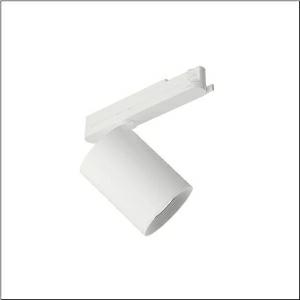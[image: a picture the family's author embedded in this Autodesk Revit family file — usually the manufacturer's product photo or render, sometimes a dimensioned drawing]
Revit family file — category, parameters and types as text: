
# Revit family: spot_21_51se13mbb5b
name_source: partatom
category: Lighting Fixtures
units: mm (PartAtom-declared; Revit-internal decimal feet)

## family parameters
Cut with Voids When Loaded = No
Host = Face
Light Source = No
Part Type = Normal
Room Calculation Point = No
Round Connector Dimension = Use Diameter
Shared = No

## types (1)
- --- (1 x LED, 5350 lm, 41.8 W, 3000K)
    Apparent Load = 42 VA
    CIE Flux Codes = 95 98 99 100 100
    Color Rendering = 90
    Color Temperature = 3000K
    Default Elevation = 1800 mm
    Description = Spot 21, directional spotlight, light control with lens, of PMMA, LED rated luminous flux: 5.140lm, light colour: 930, control gear: ECG Multilumen, with 3-phase adapter, mains connection: 220..240V, AC, 50/60Hz, of aluminium, traffic white (RAL 9016), length: 213mm, diameter: 105mm, protection rating (complete): IP20, insulation class (complete): insulation class I (protective earthing), certification: CE, impact resistance: IK02, permissible ambient temperature for indoor applications: -20..+40°C, packaging unit: 1 piece
    Height = 175 mm
    Lamp = 1 x LED
    Lamp Light Flux = 5350 lm
    Lamp Power = 41.8 W
    Lamp count = 1
    Length = 105 mm
    Luminous efficacy = 128 lm/W
    Manufacturer = Siteco
    ModVariant = No
    Model = 51SE13MBB5B
    Mounting Place = Ceiling
    Mounting Type = Pendant
    Number of Poles = 1
    OnlyDefault = Yes
    Power Factor = 1
    Product Name = Spot 21
    Product group = directional spotlight
    ProductGroupID = 904
    Protection Class = Protection class I
    Protection Degree = IP 20
    RLX_Detail_Level = 1
    RlxData = <blob elided: 17669 chars, md5=89f1b0f4>
    Socket = socket
    Standby Power = 0 W
    System Light Flux = 5350 lm
    System Power = 42 W
    Type Comments = factory setting: luminous flux: 100 % | (ON | ON | ON | ON) | 1050 mA
    Type Image = l_1003976.jpg
    URL = http://relux.com
    VarID = @adj_053373
    Voltage = 0 V
    Weight = 0.00 kg
    Width = 0 mm  [stored 0 ft]

note: [stored X ft] marks values corroborated as IEEE doubles in the binary element streams (Revit-internal decimal feet)

## geometry (parser evidence)
native form markers: Blend x4, Sweep x11
no freeform markers — native parametric forms only
